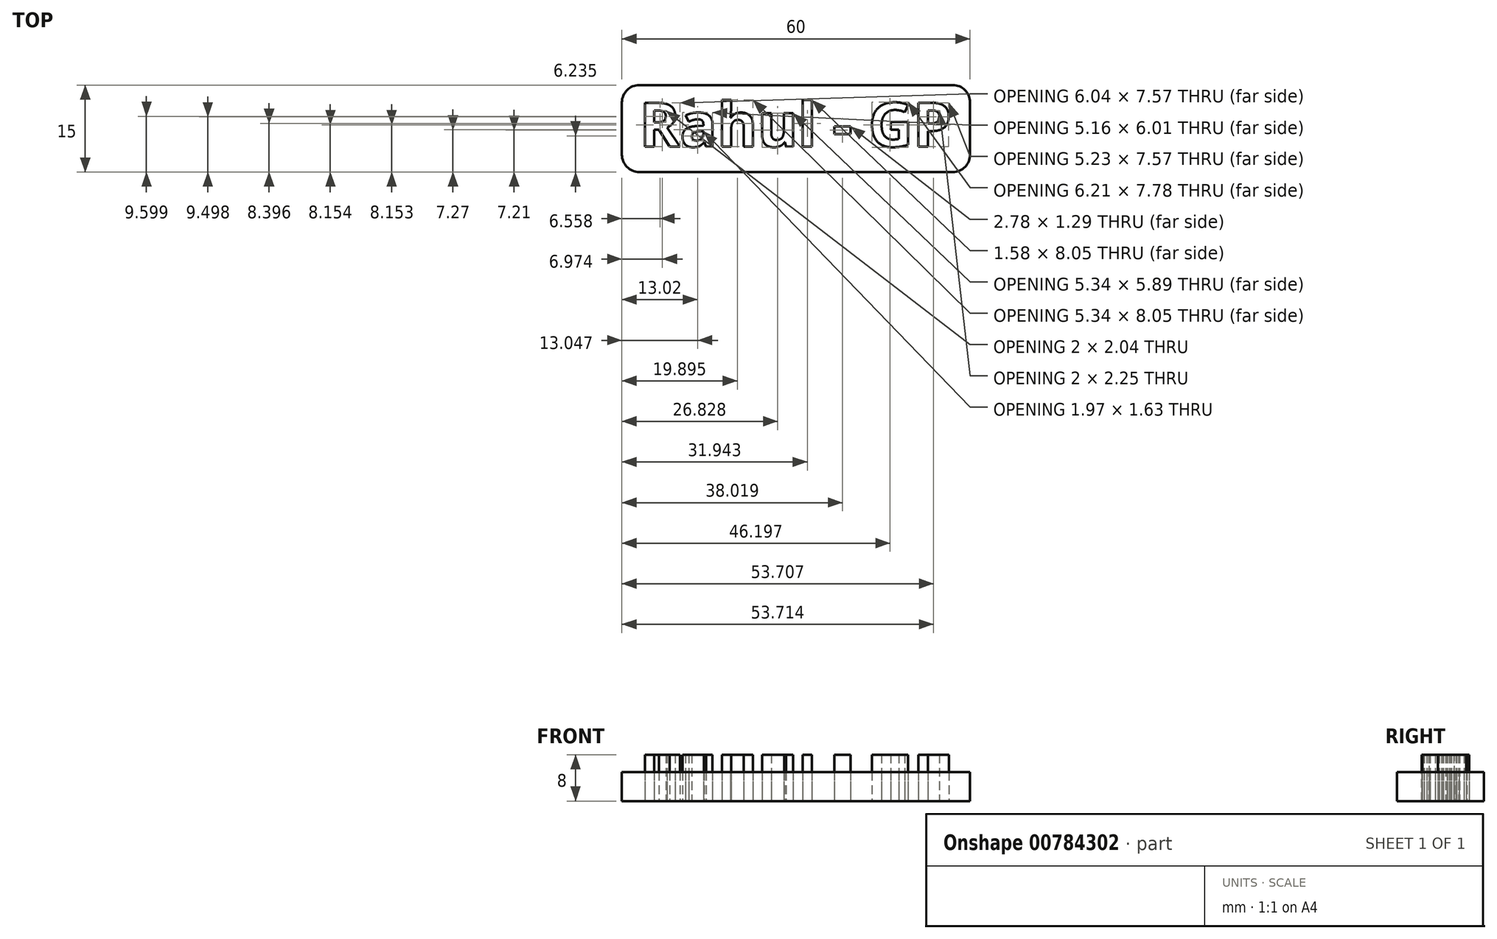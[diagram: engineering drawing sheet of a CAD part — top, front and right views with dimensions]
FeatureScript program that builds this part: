
annotation { "Feature Type Name" : "Feature", "Feature Type Description" : "" }
export const myFeature = defineFeature(function(context is Context, id is Id, definition is map)
    precondition{}
    {
        {
            var Q0;
            Q0=qCreatedBy(makeId("Top.planeOp"),FACE);
            var sketch = newSketch(context, id + "F0", { "sketchPlane" : qUnion([Q0])});
            skLineSegment(sketch, "E0.bottom", {"start": v(3, 0) * mm, "end": v(57, 0) * mm});
            skLineSegment(sketch, "E0.top", {"start": v(3, 15) * mm, "end": v(57, 15) * mm});
            skLineSegment(sketch, "E0.left", {"start": v(0, 3) * mm, "end": v(0, 12) * mm});
            skLineSegment(sketch, "E0.right", {"start": v(60, 3) * mm, "end": v(60, 12) * mm});
            skPoint(sketch, "E1.visualSharp", {"position": v(0, 15) * mm});
            skArc(sketch, "E1.filletArc", {"start": v(3, 15) * mm, "mid": v(0.88, 14.12) * mm, "end": v(0, 12) * mm});
            skPoint(sketch, "E2.visualSharp", {"position": v(0, 0) * mm});
            skArc(sketch, "E2.filletArc", {"start": v(0, 3) * mm, "mid": v(0.88, 0.88) * mm, "end": v(3, 0) * mm});
            skPoint(sketch, "E3.visualSharp", {"position": v(60, 0) * mm});
            skArc(sketch, "E3.filletArc", {"start": v(57, 0) * mm, "mid": v(59.12, 0.88) * mm, "end": v(60, 3) * mm});
            skPoint(sketch, "E4.visualSharp", {"position": v(60, 15) * mm});
            skArc(sketch, "E4.filletArc", {"start": v(60, 12) * mm, "mid": v(59.12, 14.12) * mm, "end": v(57, 15) * mm});
            skText(sketch, "E5", { "text": "Rahul - GP", "fontName": "NotoSans-Bold.ttf"});
            const initialGuessF0  = {"E5": [0.003, 0.00437, 1, 0, 0.00763]};
            skSetInitialGuess(sketch, initialGuessF0);
            skSolve(sketch);
        }
        {
            var Q0;
            Q0=makeQuery(id+"F0.imprint","IMPRINT",FACE,{"disambiguationData":[TD([[makeQuery(id+"F0.imprint","IMPRINT",EDGE,{"derivedFrom":sQuery(id+"F0.wireOp",EDGE,"E5.sketch_text.stroke-19")}),-1.0]])]});
            var Q1;
            Q1=makeQuery(id+"F0.imprint","IMPRINT",FACE,{"disambiguationData":[TD([[makeQuery(id+"F0.imprint","IMPRINT",EDGE,{"derivedFrom":sQuery(id+"F0.wireOp",EDGE,"E5.sketch_text.stroke-0")}),-1.0]])]});
            var Q2;
            Q2=makeQuery(id+"F0.imprint","IMPRINT",FACE,{"disambiguationData":[TD([[makeQuery(id+"F0.imprint","IMPRINT",EDGE,{"derivedFrom":sQuery(id+"F0.wireOp",EDGE,"E5.sketch_text.stroke-44")}),-1.0]])]});
            var Q3;
            Q3=makeQuery(id+"F0.imprint","IMPRINT",FACE,{"disambiguationData":[TD([[makeQuery(id+"F0.imprint","IMPRINT",EDGE,{"derivedFrom":sQuery(id+"F0.wireOp",EDGE,"E5.sketch_text.stroke-61")}),-1.0]])]});
            var Q4;
            Q4=makeQuery(id+"F0.imprint","IMPRINT",FACE,{"disambiguationData":[TD([[makeQuery(id+"F0.imprint","IMPRINT",EDGE,{"derivedFrom":sQuery(id+"F0.wireOp",EDGE,"E5.sketch_text.stroke-78")}),-1.0]])]});
            var Q5;
            Q5=makeQuery(id+"F0.imprint","IMPRINT",FACE,{"disambiguationData":[TD([[makeQuery(id+"F0.imprint","IMPRINT",EDGE,{"derivedFrom":sQuery(id+"F0.wireOp",EDGE,"E5.sketch_text.stroke-82")}),-1.0]])]});
            var Q6;
            Q6=makeQuery(id+"F0.imprint","IMPRINT",FACE,{"disambiguationData":[TD([[makeQuery(id+"F0.imprint","IMPRINT",EDGE,{"derivedFrom":sQuery(id+"F0.wireOp",EDGE,"E5.sketch_text.stroke-86")}),-1.0]])]});
            var Q7;
            Q7=makeQuery(id+"F0.imprint","IMPRINT",FACE,{"disambiguationData":[TD([[makeQuery(id+"F0.imprint","IMPRINT",EDGE,{"derivedFrom":sQuery(id+"F0.wireOp",EDGE,"E5.sketch_text.stroke-105")}),-1.0]])]});
            extrude(context, id + "F1", {"entities" : qUnion([Q0, Q1, Q2, Q3, Q4, Q5, Q6, Q7]), "depth" : 8 * mm, "offsetDistance" : 25 * mm});
        }
        {
            var Q0;
            Q0=makeQuery(id+"F0.imprint","IMPRINT",FACE,{"disambiguationData":[TD([[makeQuery(id+"F0.imprint","IMPRINT",EDGE,{"derivedFrom":sQuery(id+"F0.wireOp",EDGE,"E0.bottom")}),1.0]])]});
            extrude(context, id + "F2", {"entities" : qUnion([Q0]), "depth" : 5 * mm, "offsetDistance" : 25 * mm});
        }
    });
